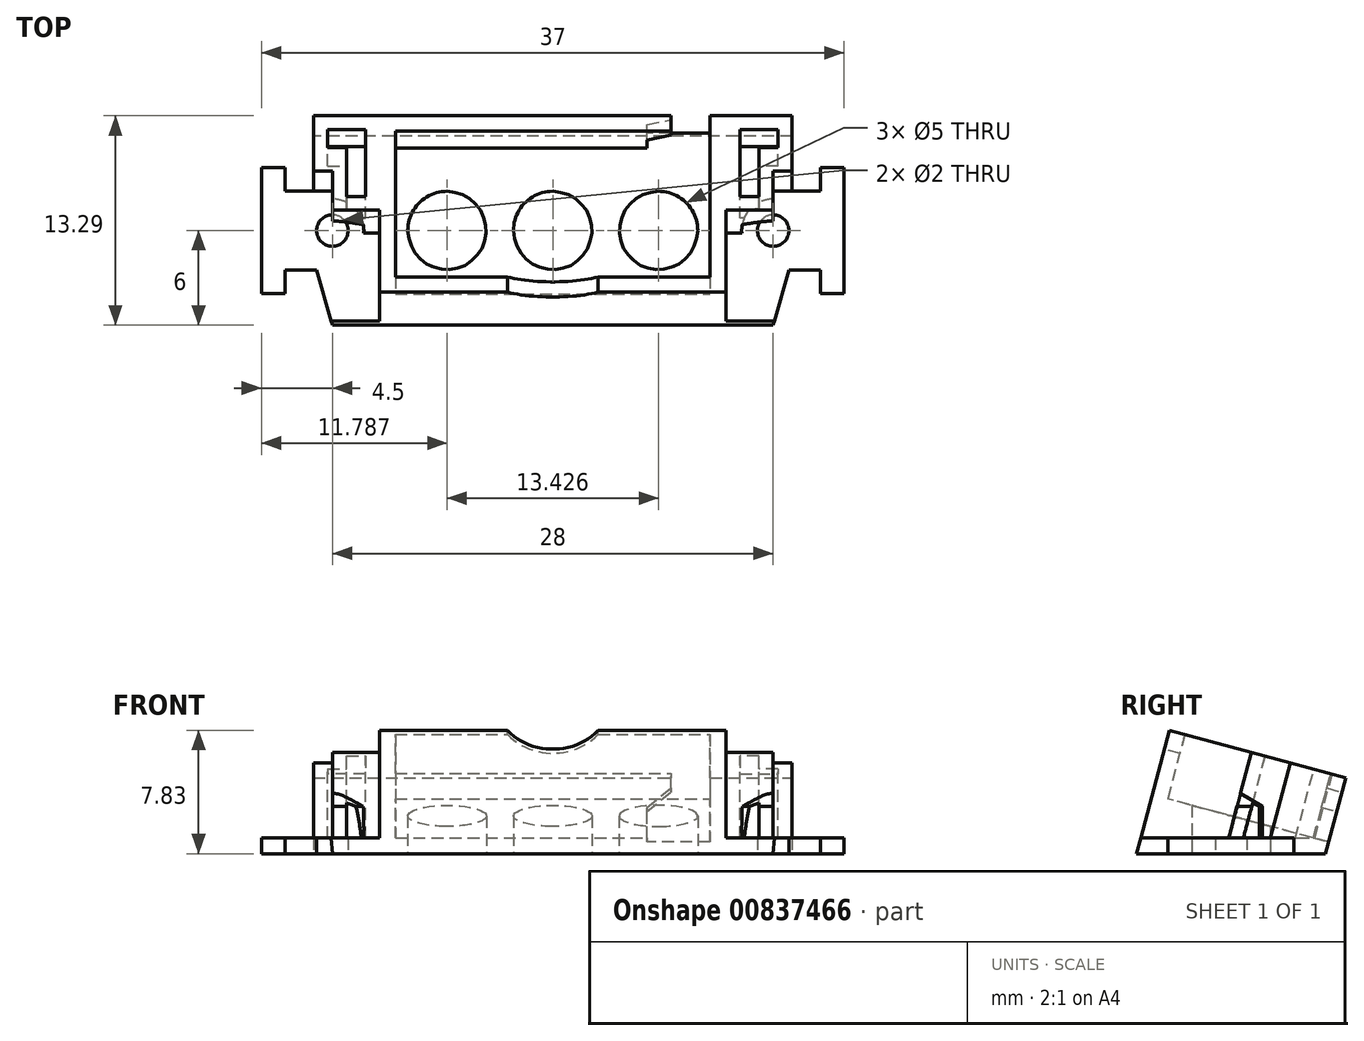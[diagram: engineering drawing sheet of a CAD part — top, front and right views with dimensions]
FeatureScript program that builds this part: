
annotation { "Feature Type Name" : "Feature", "Feature Type Description" : "" }
export const myFeature = defineFeature(function(context is Context, id is Id, definition is map)
    precondition{}
    {
        {
            var Q0;
            Q0=qCreatedBy(makeId("Top.planeOp"),FACE);
            var sketch = newSketch(context, id + "F0", { "sketchPlane" : qUnion([Q0])});
            skLineSegment(sketch, "E0", {"start": v(-18.5, 0) * mm, "end": v(-18.5, -4) * mm});
            skLineSegment(sketch, "E1", {"start": v(-18.5, -4) * mm, "end": v(-17, -4) * mm});
            skLineSegment(sketch, "E2", {"start": v(-17, -4) * mm, "end": v(-17, -2.5) * mm});
            skLineSegment(sketch, "E3", {"start": v(-17, -2.5) * mm, "end": v(-15, -2.5) * mm});
            skLineSegment(sketch, "E4", {"start": v(0, 0) * mm, "end": v(-18.5, 0) * mm, "construction": true});
            skLineSegment(sketch, "E5", {"start": v(0, -6) * mm, "end": v(-14, -6) * mm});
            skLineSegment(sketch, "E6", {"start": v(-14, -6) * mm, "end": v(-15, -2.5) * mm});
            skPoint(sketch, "E7", {"position": v(-14, 0) * mm});
            skLineSegment(sketch, "E8.MirrorCS", {"start": v(-18.5, 0) * mm, "end": v(-18.5, 4) * mm});
            skLineSegment(sketch, "E9.MirrorCS", {"start": v(-17, 2.5) * mm, "end": v(-15, 2.5) * mm});
            skLineSegment(sketch, "E10.MirrorCS", {"start": v(-18.5, 4) * mm, "end": v(-17, 4) * mm});
            skLineSegment(sketch, "E11.MirrorCS", {"start": v(-17, 4) * mm, "end": v(-17, 2.5) * mm});
            skLineSegment(sketch, "E12", {"start": v(0, 6) * mm, "end": v(0, -6) * mm});
            skPoint(sketch, "E13", {"position": v(-14, -6) * mm});
            skLineSegment(sketch, "E14.0", {"start": v(-11, 0.7) * mm, "end": v(-11, 5.2) * mm});
            skLineSegment(sketch, "E14.2", {"start": v(-13.6, 3.9) * mm, "end": v(-12.3, 3.9) * mm});
            skLineSegment(sketch, "E14.3", {"start": v(-12.3, 3.9) * mm, "end": v(-12.3, 0.7) * mm});
            skLineSegment(sketch, "E14.4", {"start": v(-12.3, 0.7) * mm, "end": v(-11, 0.7) * mm});
            skLineSegment(sketch, "E15", {"start": v(-11, 5.2) * mm, "end": v(-13.6, 5.2) * mm});
            skLineSegment(sketch, "E16", {"start": v(-13.6, 3.9) * mm, "end": v(-13.6, 5.2) * mm});
            skLineSegment(sketch, "E17.0", {"start": v(-10.2, -0.1) * mm, "end": v(-10.2, 6) * mm});
            skLineSegment(sketch, "E17.1", {"start": v(-14.4, 3.1) * mm, "end": v(-14.4, 6) * mm});
            skLineSegment(sketch, "E17.2", {"start": v(-14.4, 3.1) * mm, "end": v(-13.1, 3.1) * mm});
            skLineSegment(sketch, "E17.3", {"start": v(-10.2, 6) * mm, "end": v(-14.4, 6) * mm});
            skLineSegment(sketch, "E17.4", {"start": v(-13.1, 3.1) * mm, "end": v(-13.1, -0.1) * mm});
            skLineSegment(sketch, "E17.5", {"start": v(-13.1, -0.1) * mm, "end": v(-10.2, -0.1) * mm});
            skLineSegment(sketch, "E18", {"start": v(0, 6) * mm, "end": v(-14.4, 6) * mm});
            skLineSegment(sketch, "E19", {"start": v(-14.4, 6) * mm, "end": v(-15, 2.5) * mm});
            skPoint(sketch, "E20", {"position": v(-6.71, 0) * mm});
            skSolve(sketch);
        }
        {
            var Q0;
            Q0=makeQuery(id+"F0.imprint","IMPRINT",FACE,{"disambiguationData":[TD([[makeQuery(id+"F0.imprint","IMPRINT",EDGE,{"derivedFrom":sQuery(id+"F0.wireOp",EDGE,"E0")}),1.0]])]});
            var Q1;
            Q1=makeQuery(id+"F0.imprint","IMPRINT",FACE,{"disambiguationData":[TD([[makeQuery(id+"F0.imprint","IMPRINT",EDGE,{"derivedFrom":sQuery(id+"F0.wireOp",EDGE,"E14.0")}),1.0]])]});
            var Q2;
            {var subQ1=sQuery(id+"F0.wireOp",EDGE,"0iFpUfmZ-geOJ-y0hq-pgRL-twRDiJhUGCRu");Q2=makeQuery(id+"F0.imprint","IMPRINT",FACE,{"disambiguationData":[TD([[makeQuery(id+"F0.imprint","IMPRINT",EDGE,{"derivedFrom":subQ1}),1.0]])]});}
            var Q3;
            Q3=makeQuery(id+"F0.imprint","IMPRINT",FACE,{"disambiguationData":[TD([[makeQuery(id+"F0.imprint","IMPRINT",EDGE,{"derivedFrom":sQuery(id+"F0.wireOp",EDGE,"E14.0")}),-1.0]])]});
            extrude(context, id + "F1", {"entities" : qUnion([Q0, Q1, Q2, Q3]), "depth" : 1 * mm, "offsetDistance" : 25 * mm});
        }
        {
            var Q0;
            Q0=qCreatedBy(makeId("Right.planeOp"),FACE);
            var sketch = newSketch(context, id + "F2", { "sketchPlane" : qUnion([Q0])});
            skLineSegment(sketch, "E21", {"start": v(6, 0) * mm, "end": v(-6, 0) * mm});
            skLineSegment(sketch, "E22", {"start": v(6, 0) * mm, "end": v(7.3, 4.83) * mm});
            skLineSegment(sketch, "E23", {"start": v(7.3, 4.83) * mm, "end": v(-3.9, 7.83) * mm});
            skLineSegment(sketch, "E24", {"start": v(-6, 0) * mm, "end": v(-3.9, 7.83) * mm});
            skLineSegment(sketch, "E25", {"start": v(6.33, 5.09) * mm, "end": v(4.96, 0) * mm});
            skLineSegment(sketch, "E26", {"start": v(-2.94, 7.57) * mm, "end": v(-4.96, 0) * mm});
            skPoint(sketch, "E27", {"position": v(-4.7, 1) * mm});
            skLineSegment(sketch, "E28", {"start": v(5.23, 1) * mm, "end": v(-4.03, 3.48) * mm});
            skSolve(sketch);
        }
        {
            var Q0;
            {var subQ0=sQuery(id+"F2.wireOp",EDGE,"E24");Q0=makeQuery(id+"F2.imprint","IMPRINT",FACE,{"disambiguationData":[TD([[makeQuery(id+"F2.imprint","IMPRINT",EDGE,{"derivedFrom":subQ0}),-1.0]])]});}
            var Q1;
            {var subQ0=sQuery(id+"F2.wireOp",EDGE,"E22");Q1=makeQuery(id+"F2.imprint","IMPRINT",FACE,{"disambiguationData":[TD([[makeQuery(id+"F2.imprint","IMPRINT",EDGE,{"derivedFrom":subQ0}),1.0]])]});}
            var Q2;
            {var subQ5=sQuery(id+"F2.wireOp",EDGE,"cGWMo5V0-yn2y-PKoW-mtNu-YcyLo0oIoFNa");Q2=makeQuery(id+"F2.imprint","IMPRINT",FACE,{"disambiguationData":[TD([[makeQuery(id+"F2.imprint","IMPRINT",EDGE,{"derivedFrom":subQ5}),1.0]])]});}
            var Q3;
            {var subQ5=sQuery(id+"F2.wireOp",EDGE,"E28");Q3=makeQuery(id+"F2.imprint","IMPRINT",FACE,{"disambiguationData":[TD([[makeQuery(id+"F2.imprint","IMPRINT",EDGE,{"derivedFrom":subQ5}),1.0]])]});}
            var Q4;
            {var subQ5=sQuery(id+"F2.wireOp",EDGE,"E28");Q4=makeQuery(id+"F2.imprint","IMPRINT",FACE,{"disambiguationData":[TD([[makeQuery(id+"F2.imprint","IMPRINT",EDGE,{"derivedFrom":subQ5}),-1.0]])]});}
            extrude(context, id + "F3", {"entities" : qUnion([Q0, Q1, Q2, Q3, Q4]), "operationType" : NewBodyOperationType.ADD, "oppositeDirection" : true, "depth" : 11 * mm, "offsetDistance" : 25 * mm});
        }
        {
            var Q0;
            {var subQ5=sQuery(id+"F2.wireOp",EDGE,"E28");Q0=makeQuery(id+"F2.imprint","IMPRINT",FACE,{"disambiguationData":[TD([[makeQuery(id+"F2.imprint","IMPRINT",EDGE,{"derivedFrom":subQ5}),-1.0]])]});}
            extrude(context, id + "F4", {"entities" : qUnion([Q0]), "operationType" : NewBodyOperationType.REMOVE, "oppositeDirection" : true, "depth" : 10 * mm, "offsetDistance" : 25 * mm});
        }
        {
            var Q0;
            {var subQ4=sQuery(id+"F2.wireOp",EDGE,"E25");var subQ5=makeQuery(id+"F4.boolean.opBoolean","COPY",FACE,{"derivedFrom":makeQuery(id+"F4.opExtrude","SWEPT_FACE",FACE,{"disambiguationData":[OSD([subQ4])]})});var subQ8=sQuery(id+"F2.wireOp",EDGE,"E23");var subQ9=makeQuery(id+"F3.opExtrude","SWEPT_FACE",FACE,{"disambiguationData":[OSD([subQ8])]});Q0=makeQuery(id+"F16.boolean.opBoolean","SPLIT",FACE,{"disambiguationData":[TD([subQ5])],"derivedFrom":makeQuery(id+"F12.boolean.opBoolean","MERGE",FACE,{"derivedFrom":[subQ9,makeQuery(id+"F12.opPattern","COPY",FACE,{"derivedFrom":subQ9,"instanceName":"1"})]})});}
            var sketch = newSketch(context, id + "F5", { "sketchPlane" : qUnion([Q0])});
            skLineSegment(sketch, "E29.0", {"start": v(-11.9, 0.5) * mm, "end": v(-11.9, 4.9) * mm});
            skLineSegment(sketch, "E29.2", {"start": v(-14.3, 3.7) * mm, "end": v(-13.1, 3.7) * mm});
            skLineSegment(sketch, "E29.3", {"start": v(-13.1, 3.7) * mm, "end": v(-13.1, 0.5) * mm});
            skLineSegment(sketch, "E29.4", {"start": v(-13.1, 0.5) * mm, "end": v(-11.9, 0.5) * mm});
            skLineSegment(sketch, "E30", {"start": v(-11.9, 4.9) * mm, "end": v(-14.3, 4.9) * mm});
            skLineSegment(sketch, "E31", {"start": v(-14.3, 3.7) * mm, "end": v(-14.3, 4.9) * mm});
            skLineSegment(sketch, "E32.0", {"start": v(-15.2, 2.8) * mm, "end": v(-14, 2.8) * mm});
            skLineSegment(sketch, "E32.1", {"start": v(-14, -0.4) * mm, "end": v(-11, -0.4) * mm});
            skLineSegment(sketch, "E32.2", {"start": v(-11, -0.4) * mm, "end": v(-11, 5.8) * mm});
            skLineSegment(sketch, "E32.3", {"start": v(-14, 2.8) * mm, "end": v(-14, -0.4) * mm});
            skLineSegment(sketch, "E32.4", {"start": v(-11, 5.8) * mm, "end": v(-15.2, 5.8) * mm});
            skLineSegment(sketch, "E32.5", {"start": v(-15.2, 2.8) * mm, "end": v(-15.2, 5.8) * mm});
            skLineSegment(sketch, "E33", {"start": v(-15.2, 2.8) * mm, "end": v(-15.2, 2.16) * mm});
            skLineSegment(sketch, "E34", {"start": v(-15.2, 2.16) * mm, "end": v(-14, 2.16) * mm});
            skSolve(sketch);
        }
        {
            var Q0;
            Q0=makeQuery(id+"F5.imprint","IMPRINT",FACE,{"disambiguationData":[TD([[makeQuery(id+"F5.imprint","IMPRINT",EDGE,{"derivedFrom":sQuery(id+"F5.wireOp",EDGE,"E29.0")}),-1.0]])]});
            var Q1;
            {var subQ0=sQuery(id+"F5.wireOp",EDGE,"E32.0");Q1=makeQuery(id+"F5.imprint","IMPRINT",FACE,{"disambiguationData":[TD([[makeQuery(id+"F5.imprint","IMPRINT",EDGE,{"derivedFrom":subQ0}),-1.0]])]});}
            var Q2;
            Q2=makeQuery(id+"F1.opExtrude","CAP_FACE",FACE,{"disambiguationData":[OSD([sQuery(id+"F0.wireOp",EDGE,"E0"),sQuery(id+"F0.wireOp",EDGE,"E1"),sQuery(id+"F0.wireOp",EDGE,"E2"),sQuery(id+"F0.wireOp",EDGE,"E3"),sQuery(id+"F0.wireOp",EDGE,"E5"),sQuery(id+"F0.wireOp",EDGE,"E6"),sQuery(id+"F0.wireOp",EDGE,"E9.MirrorCS"),sQuery(id+"F0.wireOp",EDGE,"E11.MirrorCS"),sQuery(id+"F0.wireOp",EDGE,"E8.MirrorCS"),sQuery(id+"F0.wireOp",EDGE,"E10.MirrorCS"),sQuery(id+"F0.wireOp",EDGE,"E12"),sQuery(id+"F0.wireOp",EDGE,"E18"),sQuery(id+"F0.wireOp",EDGE,"E19")])],"isStart":true});
            extrude(context, id + "F6", {"entities" : qUnion([Q0, Q1]), "operationType" : NewBodyOperationType.ADD, "endBound" : BoundingType.UP_TO_SURFACE, "oppositeDirection" : true, "depth" : 25 * mm, "endBoundEntityFace" : qUnion([Q2]), "offsetDistance" : 25 * mm});
        }
        {
            var Q0;
            {var subQ0=makeQuery(id+"F1.opExtrude","CAP_EDGE",EDGE,{"disambiguationData":[OSD([sQuery(id+"F0.wireOp",EDGE,"E5")])],"isStart":false});Q0=makeQuery(id+"F12.boolean.opBoolean","MERGE",EDGE,{"derivedFrom":[subQ0,makeQuery(id+"F12.opPattern","COPY",EDGE,{"derivedFrom":subQ0,"instanceName":"1"})]});}
            chamfer(context, id + "F7", {"entities" : qUnion([Q0]), "chamferType" : ChamferType.OFFSET_ANGLE, "width" : 1 * mm, "oppositeDirection" : false, "angle" : 15 * degree, "tangentPropagation" : true});
        }
        {
            var Q0;
            Q0=sQuery(id+"F0.wireOp",VERTEX,"E7");
            var Q1;
            Q1=makeQuery(id+"F1.opExtrude","SWEPT_BODY",BODY,{"disambiguationData":[OSD([sQuery(id+"F0.wireOp",EDGE,"E0"),sQuery(id+"F0.wireOp",EDGE,"E1"),sQuery(id+"F0.wireOp",EDGE,"E2"),sQuery(id+"F0.wireOp",EDGE,"E3"),sQuery(id+"F0.wireOp",EDGE,"E5"),sQuery(id+"F0.wireOp",EDGE,"E6"),sQuery(id+"F0.wireOp",EDGE,"d604d715-9faa-478f-871a-cee185c940e80.MirrorCS"),sQuery(id+"F0.wireOp",EDGE,"E9.MirrorCS"),sQuery(id+"F0.wireOp",EDGE,"E11.MirrorCS"),sQuery(id+"F0.wireOp",EDGE,"E8.MirrorCS"),sQuery(id+"F0.wireOp",EDGE,"E10.MirrorCS"),sQuery(id+"F0.wireOp",EDGE,"d604d715-9faa-478f-871a-cee185c940e85.MirrorCS"),sQuery(id+"F0.wireOp",EDGE,"E12")])]});
            hole(context, id + "F8", {"style" : HoleStyle.SIMPLE, "endStyle" : HoleEndStyle.BLIND, "oppositeDirection" : true, "holeDiameter" : 2 * mm, "majorDiameter" : 5 * mm, "holeDepth" : 2 * mm, "isTappedThrough" : true, "tappedDepth" : 12 * mm, "tapClearance" : 3, "startFromSketch" : true, "locations" : qUnion([Q0]), "scope" : qUnion([Q1])});
        }
        {
            var Q0;
            {var subQ0=sQuery(id+"F0.wireOp",EDGE,"E10.MirrorCS");var subQ1=sQuery(id+"F0.wireOp",EDGE,"E11.MirrorCS");var subQ2=sQuery(id+"F0.wireOp",EDGE,"E9.MirrorCS");var subQ4=sQuery(id+"F0.wireOp",EDGE,"d604d715-9faa-478f-871a-cee185c940e80.MirrorCS");var subQ5=sQuery(id+"F0.wireOp",EDGE,"E6");var subQ6=sQuery(id+"F0.wireOp",EDGE,"E5");var subQ10=sQuery(id+"F0.wireOp",EDGE,"E8.MirrorCS");var subQ11=sQuery(id+"F0.wireOp",EDGE,"E0");var subQ12=sQuery(id+"F0.wireOp",EDGE,"E1");var subQ13=sQuery(id+"F0.wireOp",EDGE,"E2");var subQ14=sQuery(id+"F0.wireOp",EDGE,"E3");var subQ15=sQuery(id+"F0.wireOp",EDGE,"d604d715-9faa-478f-871a-cee185c940e85.MirrorCS");var subQ16=sQuery(id+"F0.wireOp",EDGE,"E12");Q0=makeQuery(id+"Fbzeh6eTaTLZA85_1.boolean.opBoolean","SPLIT",FACE,{"disambiguationData":[TD([makeQuery(id+"F1.opExtrude","SWEPT_FACE",FACE,{"disambiguationData":[OSD([subQ12])]})])],"derivedFrom":makeQuery(id+"F1.opExtrude","CAP_FACE",FACE,{"disambiguationData":[OSD([subQ11,subQ12,subQ13,subQ14,subQ6,subQ5,subQ4,subQ2,subQ1,subQ10,subQ0,subQ15,subQ16])],"isStart":false})});}
            var sketch = newSketch(context, id + "F9", { "sketchPlane" : qUnion([Q0])});
            skCircle(sketch, "E35", {"center": v(-14, 0) * mm, "radius": 2 * mm});
            skSolve(sketch);
        }
        {
            var Q0;
            Q0=sQuery(id+"F0.wireOp",VERTEX,"E20");
            var Q1;
            Q1=sQuery(id+"F0.wireOp",VERTEX,"E4.start");
            var Q2;
            Q2=makeQuery(id+"F1.opExtrude","SWEPT_BODY",BODY,{"disambiguationData":[OSD([sQuery(id+"F0.wireOp",EDGE,"E0"),sQuery(id+"F0.wireOp",EDGE,"E1"),sQuery(id+"F0.wireOp",EDGE,"E2"),sQuery(id+"F0.wireOp",EDGE,"E3"),sQuery(id+"F0.wireOp",EDGE,"E5"),sQuery(id+"F0.wireOp",EDGE,"E6"),sQuery(id+"F0.wireOp",EDGE,"E9.MirrorCS"),sQuery(id+"F0.wireOp",EDGE,"E11.MirrorCS"),sQuery(id+"F0.wireOp",EDGE,"E8.MirrorCS"),sQuery(id+"F0.wireOp",EDGE,"E10.MirrorCS"),sQuery(id+"F0.wireOp",EDGE,"E12"),sQuery(id+"F0.wireOp",EDGE,"E17.0"),sQuery(id+"F0.wireOp",EDGE,"E17.1"),sQuery(id+"F0.wireOp",EDGE,"E17.2"),sQuery(id+"F0.wireOp",EDGE,"E17.4"),sQuery(id+"F0.wireOp",EDGE,"E17.5"),sQuery(id+"F0.wireOp",EDGE,"E18"),sQuery(id+"F0.wireOp",EDGE,"E19")])]});
            hole(context, id + "F10", {"style" : HoleStyle.SIMPLE, "endStyle" : HoleEndStyle.BLIND, "oppositeDirection" : true, "holeDiameter" : 5 * mm, "majorDiameter" : 5 * mm, "holeDepth" : 5 * mm, "isTappedThrough" : true, "tappedDepth" : 12 * mm, "tapClearance" : 3, "startFromSketch" : true, "locations" : qUnion([Q0, Q1]), "scope" : qUnion([Q2])});
        }
        {
            var Q0;
            Q0=sQuery(id+"F9.wireOp",VERTEX,"E35.center");
            var Q1;
            Q1=makeQuery(id+"F1.opExtrude","SWEPT_BODY",BODY,{"disambiguationData":[OSD([sQuery(id+"F0.wireOp",EDGE,"E0"),sQuery(id+"F0.wireOp",EDGE,"E1"),sQuery(id+"F0.wireOp",EDGE,"E2"),sQuery(id+"F0.wireOp",EDGE,"E3"),sQuery(id+"F0.wireOp",EDGE,"E5"),sQuery(id+"F0.wireOp",EDGE,"E6"),sQuery(id+"F0.wireOp",EDGE,"E9.MirrorCS"),sQuery(id+"F0.wireOp",EDGE,"E11.MirrorCS"),sQuery(id+"F0.wireOp",EDGE,"E8.MirrorCS"),sQuery(id+"F0.wireOp",EDGE,"E10.MirrorCS"),sQuery(id+"F0.wireOp",EDGE,"E12"),sQuery(id+"F0.wireOp",EDGE,"E18"),sQuery(id+"F0.wireOp",EDGE,"E19")])]});
            hole(context, id + "F11", {"style" : HoleStyle.SIMPLE, "endStyle" : HoleEndStyle.BLIND, "oppositeDirection" : true, "holeDiameter" : 4 * mm, "majorDiameter" : 5 * mm, "holeDepth" : 2 * mm, "isTappedThrough" : true, "tappedDepth" : 12 * mm, "tapClearance" : 3, "startFromSketch" : true, "locations" : qUnion([Q0]), "scope" : qUnion([Q1])});
        }
        {
            var Q0;
            Q0=makeQuery(id+"F1.opExtrude","SWEPT_BODY",BODY,{"disambiguationData":[OSD([sQuery(id+"F0.wireOp",EDGE,"E0"),sQuery(id+"F0.wireOp",EDGE,"E1"),sQuery(id+"F0.wireOp",EDGE,"E2"),sQuery(id+"F0.wireOp",EDGE,"E3"),sQuery(id+"F0.wireOp",EDGE,"E5"),sQuery(id+"F0.wireOp",EDGE,"E6"),sQuery(id+"F0.wireOp",EDGE,"d604d715-9faa-478f-871a-cee185c940e80.MirrorCS"),sQuery(id+"F0.wireOp",EDGE,"E9.MirrorCS"),sQuery(id+"F0.wireOp",EDGE,"E11.MirrorCS"),sQuery(id+"F0.wireOp",EDGE,"E8.MirrorCS"),sQuery(id+"F0.wireOp",EDGE,"E10.MirrorCS"),sQuery(id+"F0.wireOp",EDGE,"d604d715-9faa-478f-871a-cee185c940e85.MirrorCS"),sQuery(id+"F0.wireOp",EDGE,"E12")])]});
            var Q1;
            Q1=qCreatedBy(makeId("Right.planeOp"),FACE);
            mirror(context, id + "F12", {"operationType" : NewBodyOperationType.ADD, "entities" : qUnion([Q0]), "mirrorPlane" : qUnion([Q1])});
        }
        {
            var Q0;
            {var subQ0=makeQuery(id+"F3.opExtrude","SWEPT_FACE",FACE,{"disambiguationData":[OSD([sQuery(id+"F2.wireOp",EDGE,"E24")])]});Q0=makeQuery(id+"F12.boolean.opBoolean","MERGE",FACE,{"derivedFrom":[subQ0,makeQuery(id+"F12.opPattern","COPY",FACE,{"derivedFrom":subQ0,"instanceName":"1"})]});}
            var sketch = newSketch(context, id + "F13", { "sketchPlane" : qUnion([Q0])});
            skCircle(sketch, "E36", {"center": v(0, 9.32) * mm, "radius": 4 * mm});
            skSolve(sketch);
        }
        {
            var Q0;
            {var subQ0=sQuery(id+"F13.wireOp",EDGE,"E36");var subQ1=makeQuery(id+"F3.opExtrude","SWEPT_EDGE",EDGE,{"disambiguationData":[OSD([sQuery(id+"F2.wireOp",EDGE,"E23"),sQuery(id+"F2.wireOp",EDGE,"E24")])]});var subQ2=makeQuery(id+"F12.boolean.opBoolean","MERGE",EDGE,{"derivedFrom":[subQ1,makeQuery(id+"F12.opPattern","COPY",EDGE,{"derivedFrom":subQ1,"instanceName":"1"})]});var subQ3=makeQuery(id+"F13.imprint","INTERSECT",VERTEX,{"disambiguationData":[OD(0.0)],"derivedFrom":[subQ2,subQ0]});Q0=makeQuery(id+"F13.imprint","IMPRINT",FACE,{"disambiguationData":[TD([[makeQuery(id+"F13.imprint","IMPRINT",EDGE,{"disambiguationData":[TD([[subQ3,-1.0]])],"derivedFrom":subQ0}),1.0]])]});}
            extrude(context, id + "F14", {"entities" : qUnion([Q0]), "operationType" : NewBodyOperationType.REMOVE, "oppositeDirection" : true, "depth" : 1 * mm, "offsetDistance" : 25 * mm});
        }
        {
            var Q0;
            {var subQ0=makeQuery(id+"F3.opExtrude","SWEPT_FACE",FACE,{"disambiguationData":[OSD([sQuery(id+"F2.wireOp",EDGE,"E22")])]});Q0=makeQuery(id+"F12.boolean.opBoolean","MERGE",FACE,{"derivedFrom":[subQ0,makeQuery(id+"F12.opPattern","COPY",FACE,{"derivedFrom":subQ0,"instanceName":"1"})]});}
            var sketch = newSketch(context, id + "F15", { "sketchPlane" : qUnion([Q0])});
            skLineSegment(sketch, "E37", {"start": v(-10, 6.55) * mm, "end": v(-10, 2.32) * mm});
            skLineSegment(sketch, "E38", {"start": v(-10, 2.32) * mm, "end": v(-6, 2.32) * mm});
            skLineSegment(sketch, "E39", {"start": v(-6, 2.32) * mm, "end": v(-6, 4.32) * mm});
            skLineSegment(sketch, "E40", {"start": v(-6, 4.32) * mm, "end": v(-7.5, 5.6) * mm});
            skLineSegment(sketch, "E41", {"start": v(-7.5, 5.6) * mm, "end": v(-7.5, 6.55) * mm});
            skSolve(sketch);
        }
        {
            var Q0;
            {var subQ0=sQuery(id+"F15.wireOp",EDGE,"E37");Q0=makeQuery(id+"F15.imprint","IMPRINT",FACE,{"disambiguationData":[TD([[makeQuery(id+"F15.imprint","IMPRINT",EDGE,{"derivedFrom":subQ0}),1.0]])]});}
            extrude(context, id + "F16", {"entities" : qUnion([Q0]), "operationType" : NewBodyOperationType.REMOVE, "endBound" : BoundingType.UP_TO_NEXT, "oppositeDirection" : true, "depth" : 25 * mm, "offsetDistance" : 25 * mm});
        }
    });
